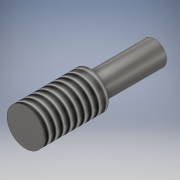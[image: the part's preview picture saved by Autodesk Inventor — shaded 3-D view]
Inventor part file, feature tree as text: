
AUTODESK INVENTOR PART (.ipt)
format: ipt  version: 2017 SP1 (Build 210196100, 196)  size: 112,640 bytes
history: native  units: in
note: dims shown in document units (in); Inventor stores cm internally (conversion verified against a paired STEP export)
features: extrude x2, thread x2, sketch x2
ambient origin geometry x8: Origin, YZ Plane, XZ Plane, XY Plane, X Axis, Y Axis, Z Axis, Center Point
bodies: Solid1 (feature_tree)
feature tree (6):
  extrude  "Extrusion1"  Depth=0.375in TaperAngle=0.0deg
  extrude  "Extrusion2"  Depth=0.375in TaperAngle=0.0deg
  thread  "Thread1"  [1 undecoded]
  thread  "Thread2"  [1 undecoded]
  sketch  "Sketch1"  dims[d0=0.216in d1=0.375in d2=0.0in]
  sketch  "Sketch2"  dims[d3=0.141in d4=0.375in d5=0.0in d6=0.375in d7=0.0469in d8=0.375in d9=0.0in]
note: 2 required parameter values undecoded (feature->parameter linkage not recoverable at this tier; creation-order binding heuristic only, values carry confidence <= 0.55)
